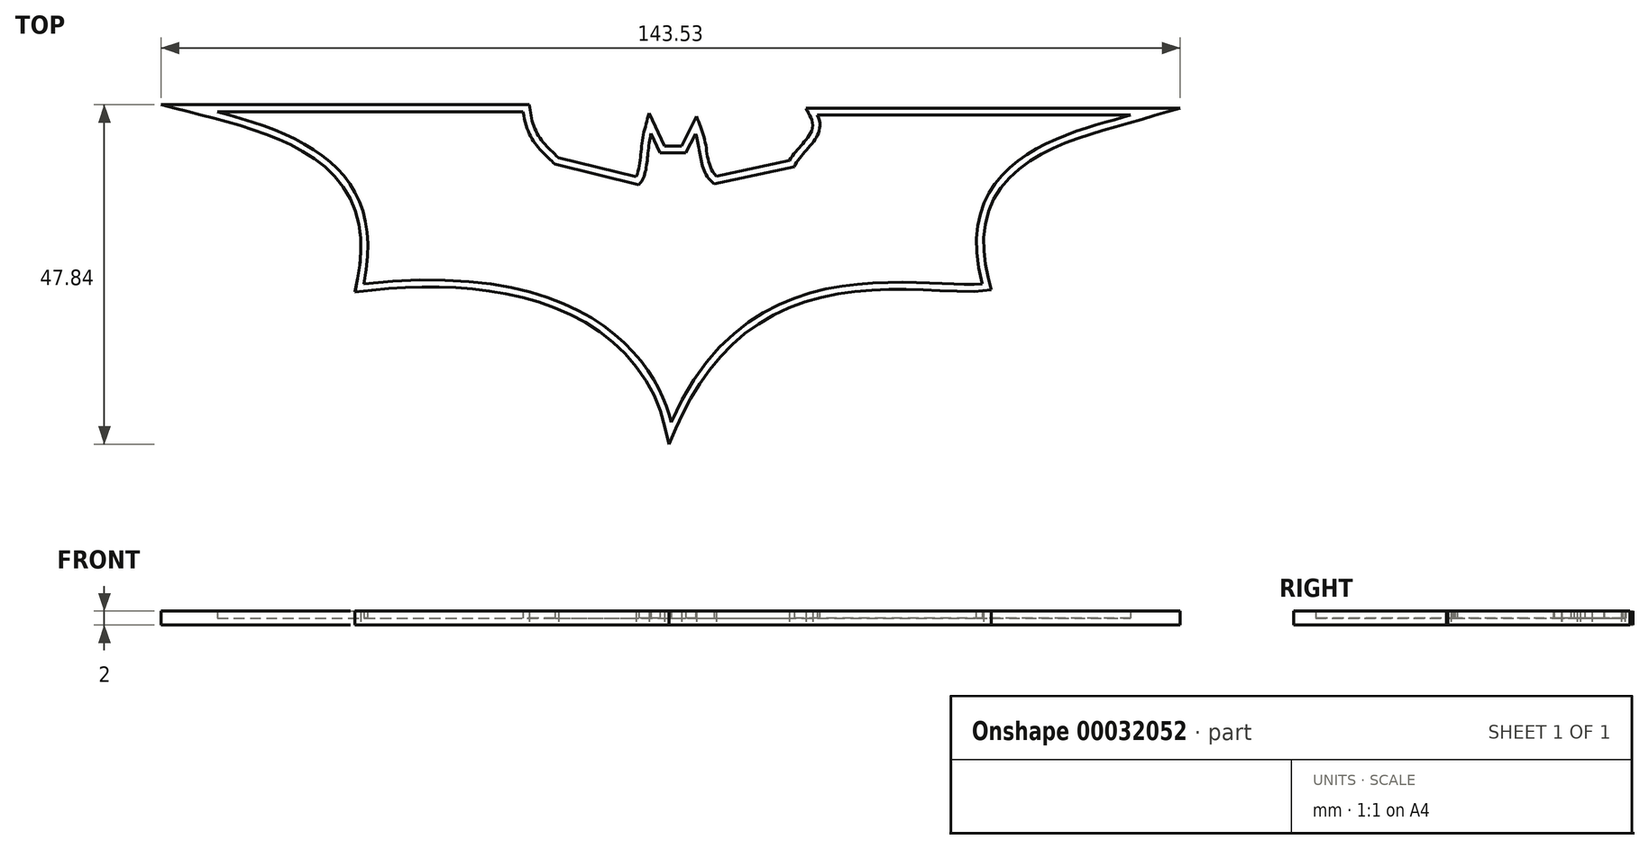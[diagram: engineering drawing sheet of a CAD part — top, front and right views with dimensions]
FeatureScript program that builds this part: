
annotation { "Feature Type Name" : "Feature", "Feature Type Description" : "" }
export const myFeature = defineFeature(function(context is Context, id is Id, definition is map)
    precondition{}
    {
        {
            var Q0;
            Q0=qCreatedBy(makeId("Top.planeOp"),FACE);
            var sketch = newSketch(context, id + "F0", { "sketchPlane" : qUnion([Q0])});
            skLineSegment(sketch, "E0", {"start": v(-78.17, 19.48) * mm, "end": v(-35.1, 19.48) * mm});
            skLineSegment(sketch, "E1", {"start": v(-30.61, 12.13) * mm, "end": v(-18.78, 9.23) * mm});
            skLineSegment(sketch, "E2", {"start": v(-10.8, 16.37) * mm, "end": v(-12.19, 13.7) * mm});
            skLineSegment(sketch, "E3", {"start": v(-8.18, 9.35) * mm, "end": v(3.1, 11.73) * mm});
            skLineSegment(sketch, "E4", {"start": v(50.5, 19.02) * mm, "end": v(6.35, 19.02) * mm});
            skLineSegment(sketch, "E5", {"start": v(-15.8, 13.7) * mm, "end": v(-17.1, 16.42) * mm});
            skFitSpline(sketch, "E6", {"points": [v(-78.17, 19.48) * mm, v(-57.53, -4.74) * mm], "startDerivative": vector(38.81, -9.96) * mm, "endDerivative": vector(-9.58, -46.82) * mm});
            skFitSpline(sketch, "E7", {"points": [v(-57.53, -4.74) * mm, v(-14.26, -24.25) * mm], "startDerivative": vector(96.47, 10.64) * mm, "endDerivative": vector(6.03, -24.47) * mm});
            skFitSpline(sketch, "E8", {"points": [v(-14.26, -24.25) * mm, v(29.6, -4.74) * mm], "startDerivative": vector(33.34, 76.61) * mm, "endDerivative": vector(25.18, 2.84) * mm});
            skFitSpline(sketch, "E9", {"points": [v(29.6, -4.74) * mm, v(50.5, 19.02) * mm], "startDerivative": vector(-14.54, 54.27) * mm, "endDerivative": vector(24.03, 7.08) * mm});
            skFitSpline(sketch, "E10", {"points": [v(6.35, 19.02) * mm, v(3.1, 11.73) * mm], "startDerivative": vector(4.49, -9.2) * mm, "endDerivative": vector(-3.26, -7.29) * mm});
            skFitSpline(sketch, "E11", {"points": [v(-10.8, 16.37) * mm, v(-8.18, 9.35) * mm], "startDerivative": vector(2.63, -7.01) * mm, "endDerivative": vector(6.9, -5.25) * mm});
            skFitSpline(sketch, "E12", {"points": [v(-17.1, 16.42) * mm, v(-18.78, 9.23) * mm], "startDerivative": vector(-1.93, -7.42) * mm, "endDerivative": vector(-4.35, -4.57) * mm});
            skFitSpline(sketch, "E13", {"points": [v(-30.61, 12.13) * mm, v(-35.1, 19.48) * mm], "startDerivative": vector(-5.18, 4.94) * mm, "endDerivative": vector(-1.45, 12.03) * mm});
            skLineSegment(sketch, "E14", {"start": v(-15.8, 13.7) * mm, "end": v(-12.19, 13.7) * mm});
            skSolve(sketch);
        }
        {
            var Q0;
            Q0=makeQuery(id+"F0.imprint","IMPRINT",FACE,{"disambiguationData":[TD([[makeQuery(id+"F0.imprint","IMPRINT",EDGE,{"derivedFrom":sQuery(id+"F0.wireOp",EDGE,"E0")}),-1.0]])]});
            extrude(context, id + "F1", {"entities" : qUnion([Q0]), "depth" : 1 * mm});
        }
        {
            var Q0;
            Q0=makeQuery(id+"F1.opExtrude","CAP_FACE",FACE,{"disambiguationData":[OSD([sQuery(id+"F0.wireOp",EDGE,"E0"),sQuery(id+"F0.wireOp",EDGE,"E1"),sQuery(id+"F0.wireOp",EDGE,"E2"),sQuery(id+"F0.wireOp",EDGE,"E3"),sQuery(id+"F0.wireOp",EDGE,"E4"),sQuery(id+"F0.wireOp",EDGE,"E5"),sQuery(id+"F0.wireOp",EDGE,"E6"),sQuery(id+"F0.wireOp",EDGE,"E7"),sQuery(id+"F0.wireOp",EDGE,"E8"),sQuery(id+"F0.wireOp",EDGE,"E9"),sQuery(id+"F0.wireOp",EDGE,"E10"),sQuery(id+"F0.wireOp",EDGE,"E11"),sQuery(id+"F0.wireOp",EDGE,"E12"),sQuery(id+"F0.wireOp",EDGE,"E13"),sQuery(id+"F0.wireOp",EDGE,"E14")])],"isStart":false});
            shell(context, id + "F2", {"entities" : qUnion([Q0]), "thickness" : 1 * mm, "oppositeDirection" : true});
        }
    });
